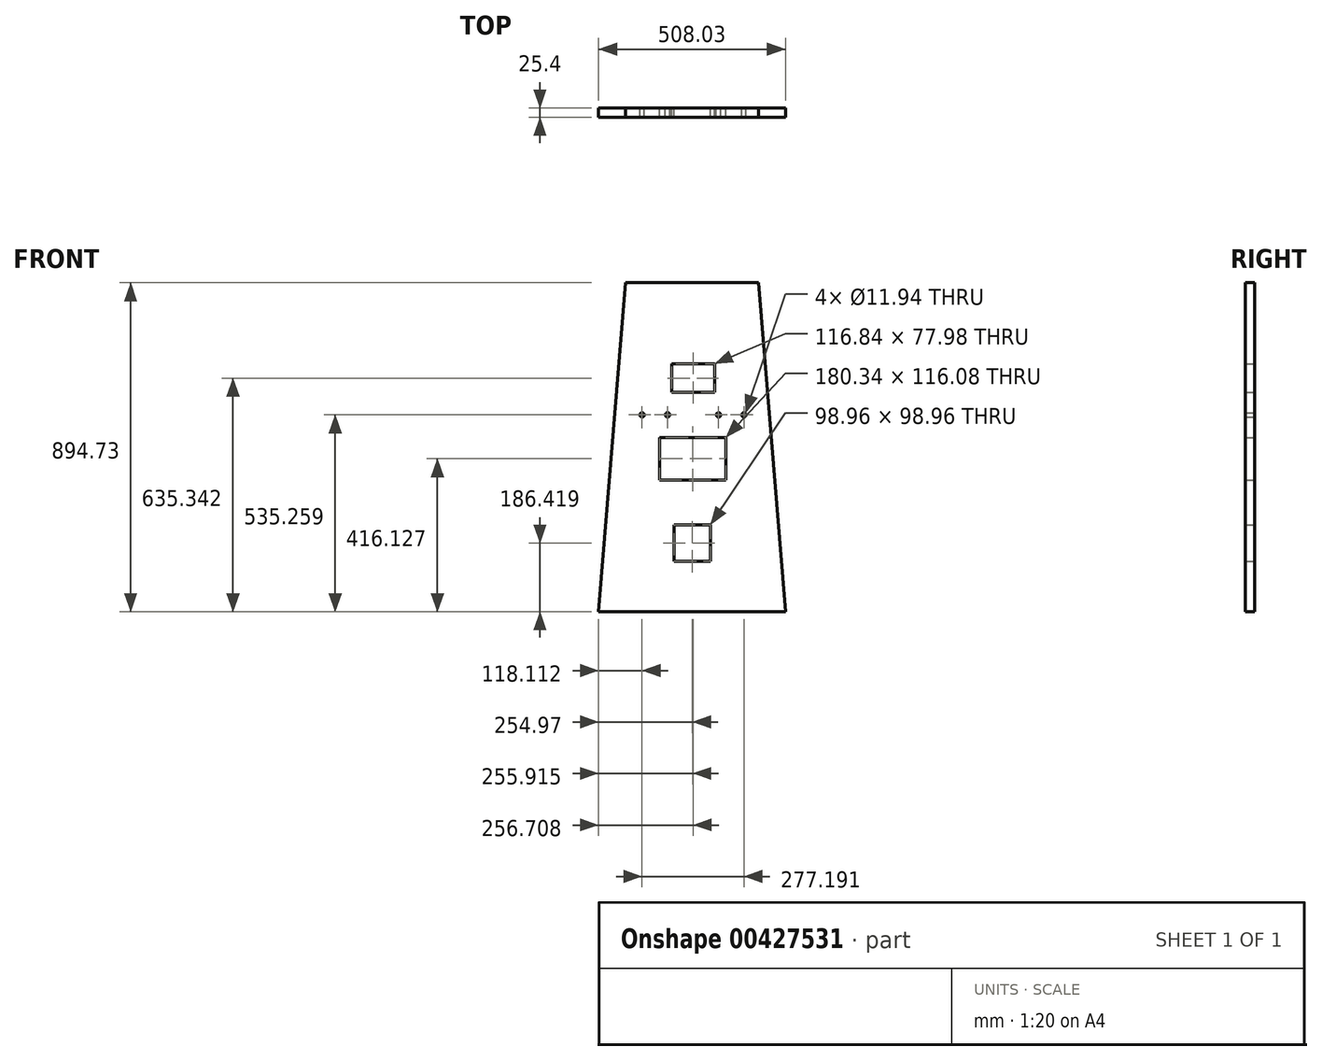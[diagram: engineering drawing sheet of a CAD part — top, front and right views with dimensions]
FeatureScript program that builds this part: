
annotation { "Feature Type Name" : "Feature", "Feature Type Description" : "" }
export const myFeature = defineFeature(function(context is Context, id is Id, definition is map)
    precondition{}
    {
        {
            var Q0;
            Q0=qCreatedBy(makeId("Front.planeOp"),FACE);
            var sketch = newSketch(context, id + "F0", { "sketchPlane" : qUnion([Q0])});
            skLineSegment(sketch, "E0.bottom", {"start": v(-97.28, 248.4) * mm, "end": v(19.56, 248.4) * mm});
            skLineSegment(sketch, "E0.top", {"start": v(-97.28, 170.42) * mm, "end": v(19.56, 170.42) * mm});
            skLineSegment(sketch, "E0.left", {"start": v(-97.28, 248.4) * mm, "end": v(-97.28, 170.42) * mm});
            skLineSegment(sketch, "E0.right", {"start": v(19.56, 248.4) * mm, "end": v(19.56, 170.42) * mm});
            skLineSegment(sketch, "E1", {"start": v(-97.28, 248.4) * mm, "end": v(-235.46, 248.4) * mm, "construction": true});
            skLineSegment(sketch, "E2", {"start": v(19.56, 248.4) * mm, "end": v(157.74, 248.4) * mm, "construction": true});
            skLineSegment(sketch, "E3.bottom", {"start": v(-129.83, 48.24) * mm, "end": v(50.51, 48.24) * mm});
            skLineSegment(sketch, "E3.top", {"start": v(-129.83, -67.84) * mm, "end": v(50.51, -67.84) * mm});
            skLineSegment(sketch, "E3.left", {"start": v(-129.83, 48.24) * mm, "end": v(-129.83, -67.84) * mm});
            skLineSegment(sketch, "E3.right", {"start": v(50.51, 48.24) * mm, "end": v(50.51, -67.84) * mm});
            skLineSegment(sketch, "E4", {"start": v(-129.83, 48.24) * mm, "end": v(-253.3, 48.24) * mm, "construction": true});
            skLineSegment(sketch, "E5", {"start": v(50.51, 48.24) * mm, "end": v(174, 48.24) * mm, "construction": true});
            skLineSegment(sketch, "E6.bottom", {"start": v(-90.08, -190.03) * mm, "end": v(8.88, -190.03) * mm});
            skLineSegment(sketch, "E6.top", {"start": v(-90.08, -289) * mm, "end": v(8.88, -289) * mm});
            skLineSegment(sketch, "E6.left", {"start": v(-90.08, -190.03) * mm, "end": v(-90.08, -289) * mm});
            skLineSegment(sketch, "E6.right", {"start": v(8.88, -190.03) * mm, "end": v(8.88, -289) * mm});
            skLineSegment(sketch, "E7", {"start": v(-90.08, -190.03) * mm, "end": v(-274.54, -190.03) * mm, "construction": true});
            skLineSegment(sketch, "E8", {"start": v(8.88, -190.03) * mm, "end": v(193.34, -190.03) * mm, "construction": true});
            skLineSegment(sketch, "E9", {"start": v(-38.86, 170.42) * mm, "end": v(-38.86, 48.24) * mm, "construction": true});
            skLineSegment(sketch, "E10", {"start": v(-39.66, -67.84) * mm, "end": v(-39.66, -190.03) * mm, "construction": true});
            skLineSegment(sketch, "E11", {"start": v(132.95, 415.46) * mm, "end": v(142.35, 415.46) * mm, "construction": true});
            skLineSegment(sketch, "E12", {"start": v(-211.2, 415.46) * mm, "end": v(-220.6, 415.46) * mm, "construction": true});
            skCircle(sketch, "E13", {"center": v(30.44, 109.33) * mm, "radius": 5.97 * mm});
            skCircle(sketch, "E14", {"center": v(99.73, 109.33) * mm, "radius": 5.97 * mm});
            skLineSegment(sketch, "E15", {"start": v(30.44, 109.33) * mm, "end": v(-38.86, 109.33) * mm, "construction": true});
            skLineSegment(sketch, "E16", {"start": v(30.44, 109.33) * mm, "end": v(99.73, 109.33) * mm, "construction": true});
            skLineSegment(sketch, "E17", {"start": v(99.73, 109.33) * mm, "end": v(169.03, 109.33) * mm, "construction": true});
            skCircle(sketch, "E18.MirrorC", {"center": v(-177.46, 109.33) * mm, "radius": 5.97 * mm});
            skCircle(sketch, "E19.MirrorC", {"center": v(-108.16, 109.33) * mm, "radius": 5.97 * mm});
            skLineSegment(sketch, "E20", {"start": v(-222.92, 468.8) * mm, "end": v(-295.57, -425.93) * mm});
            skLineSegment(sketch, "E21", {"start": v(-295.57, -425.93) * mm, "end": v(212.46, -425.93) * mm});
            skLineSegment(sketch, "E22", {"start": v(212.46, -425.93) * mm, "end": v(139.8, 468.8) * mm});
            skLineSegment(sketch, "E23", {"start": v(139.8, 468.8) * mm, "end": v(-222.92, 468.8) * mm});
            skSolve(sketch);
        }
        {
            var Q0;
            Q0 = qSketchRegion(id + "F0", true);
            extrude(context, id + "F1", {"entities" : qUnion([Q0]), "depth" : 25.4 * mm});
        }
    });
